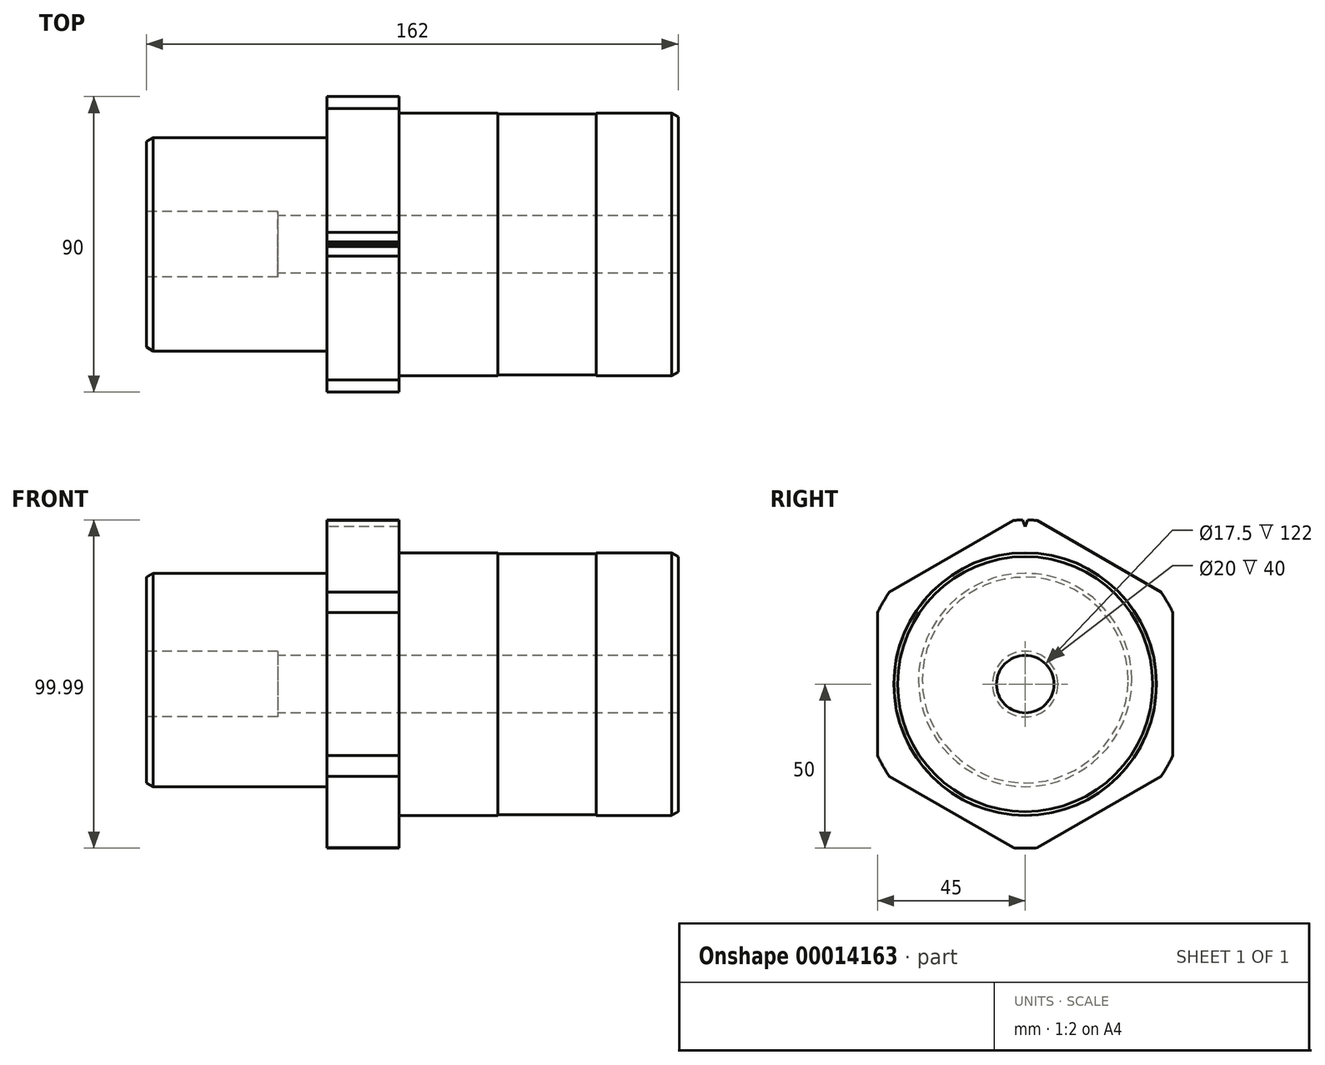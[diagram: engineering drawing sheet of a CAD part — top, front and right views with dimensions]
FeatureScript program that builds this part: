
annotation { "Feature Type Name" : "Feature", "Feature Type Description" : "" }
export const myFeature = defineFeature(function(context is Context, id is Id, definition is map)
    precondition{}
    {
        {
            var Q0;
            Q0=qCreatedBy(makeId("Right.planeOp"),FACE);
            var sketch = newSketch(context, id + "F0", { "sketchPlane" : qUnion([Q0])});
            skCircle(sketch, "E0", {"center": v(0, 0) * mm, "radius": 40 * mm});
            skCircle(sketch, "E1", {"center": v(0, 0) * mm, "radius": 8.75 * mm});
            skSolve(sketch);
        }
        {
            var Q0;
            Q0 = qSketchRegion(id + "F0", true);
            extrude(context, id + "F1", {"entities" : qUnion([Q0]), "depth" : (85 - 60) * mm});
        }
        {
            var Q0;
            Q0=makeQuery(id+"F1.opExtrude","CAP_FACE",FACE,{"disambiguationData":[OSD([sQuery(id+"F0.wireOp",EDGE,"E0"),sQuery(id+"F0.wireOp",EDGE,"E1")])],"isStart":true});
            var sketch = newSketch(context, id + "F2", { "sketchPlane" : qUnion([Q0])});
            skCircle(sketch, "E2", {"center": v(0, 0) * mm, "radius": 39.75 * mm});
            skCircle(sketch, "E3.0", {"center": v(0, 0) * mm, "radius": 8.75 * mm});
            skSolve(sketch);
        }
        {
            var Q0;
            Q0 = qSketchRegion(id + "F2", true);
            extrude(context, id + "F3", {"entities" : qUnion([Q0]), "operationType" : NewBodyOperationType.ADD, "depth" : 30 * mm});
        }
        {
            var Q0;
            Q0=makeQuery(id+"F3.opExtrude","CAP_FACE",FACE,{"disambiguationData":[OSD([sQuery(id+"F2.wireOp",EDGE,"E2"),sQuery(id+"F2.wireOp",EDGE,"E3.0")])],"isStart":false});
            var sketch = newSketch(context, id + "F4", { "sketchPlane" : qUnion([Q0])});
            skCircle(sketch, "E4", {"center": v(0, 0) * mm, "radius": 40 * mm});
            skCircle(sketch, "E5.0", {"center": v(0, 0) * mm, "radius": 8.75 * mm});
            skSolve(sketch);
        }
        {
            var Q0;
            Q0 = qSketchRegion(id + "F4", true);
            extrude(context, id + "F5", {"entities" : qUnion([Q0]), "operationType" : NewBodyOperationType.ADD, "depth" : 30 * mm});
        }
        {
            var Q0;
            Q0=makeQuery(id+"F5.opExtrude","CAP_FACE",FACE,{"disambiguationData":[OSD([sQuery(id+"F4.wireOp",EDGE,"E4"),sQuery(id+"F4.wireOp",EDGE,"E5.0")])],"isStart":false});
            var sketch = newSketch(context, id + "F6", { "sketchPlane" : qUnion([Q0])});
            skCircle(sketch, "E6.cCircle", {"center": v(0, 0) * mm, "radius": 45 * mm, "construction": true});
            skLineSegment(sketch, "E6.0", {"start": v(-45, -21.8) * mm, "end": v(-45, 21.8) * mm});
            skLineSegment(sketch, "E6.1", {"start": v(-41.37, 28.07) * mm, "end": v(-3.63, 49.87) * mm});
            skLineSegment(sketch, "E6.2", {"start": v(3.63, 49.87) * mm, "end": v(41.37, 28.07) * mm});
            skLineSegment(sketch, "E6.3", {"start": v(45, 21.8) * mm, "end": v(45, -21.8) * mm});
            skLineSegment(sketch, "E6.4", {"start": v(41.37, -28.07) * mm, "end": v(3.63, -49.87) * mm});
            skLineSegment(sketch, "E6.5", {"start": v(-3.63, -49.87) * mm, "end": v(-41.37, -28.07) * mm});
            skPoint(sketch, "E6.0.midPoint", {"position": v(-45, 0) * mm});
            skCircle(sketch, "E7.0", {"center": v(0, 0) * mm, "radius": 8.75 * mm});
            skArc(sketch, "E8", {"start": v(-3.63, -49.87) * mm, "mid": v(0, -50) * mm, "end": v(3.63, -49.87) * mm});
            skPoint(sketch, "E9.orphan", {"position": v(-45, -25.98) * mm});
            skArc(sketch, "E10.trimOffspring", {"start": v(-45, -21.8) * mm, "mid": v(-43.3, -25) * mm, "end": v(-41.37, -28.07) * mm});
            skPoint(sketch, "E11.orphan", {"position": v(-45, 25.98) * mm});
            skArc(sketch, "E12.trimOffspring", {"start": v(-41.37, 28.07) * mm, "mid": v(-43.3, 25) * mm, "end": v(-45, 21.8) * mm});
            skPoint(sketch, "E13.orphan", {"position": v(0, 51.96) * mm});
            skArc(sketch, "E14.trimOffspring", {"start": v(3.63, 49.87) * mm, "mid": v(0, 50) * mm, "end": v(-3.63, 49.87) * mm});
            skPoint(sketch, "E15.orphan", {"position": v(45, 25.98) * mm});
            skArc(sketch, "E16.trimOffspring", {"start": v(45, 21.8) * mm, "mid": v(43.3, 25) * mm, "end": v(41.37, 28.07) * mm});
            skPoint(sketch, "E17.orphan", {"position": v(45, -25.98) * mm});
            skArc(sketch, "E18.trimOffspring", {"start": v(41.37, -28.07) * mm, "mid": v(43.3, -25) * mm, "end": v(45, -21.8) * mm});
            skPoint(sketch, "E19.orphan", {"position": v(0, -51.96) * mm});
            skSolve(sketch);
        }
        {
            var Q0;
            Q0 = qSketchRegion(id + "F6", true);
            extrude(context, id + "F7", {"entities" : qUnion([Q0]), "operationType" : NewBodyOperationType.ADD, "depth" : 22 * mm});
        }
        {
            var Q0;
            Q0=makeQuery(id+"F7.opExtrude","CAP_FACE",FACE,{"disambiguationData":[OSD([sQuery(id+"F6.wireOp",EDGE,"E6.0"),sQuery(id+"F6.wireOp",EDGE,"E6.1"),sQuery(id+"F6.wireOp",EDGE,"E6.2"),sQuery(id+"F6.wireOp",EDGE,"E6.3"),sQuery(id+"F6.wireOp",EDGE,"E6.4"),sQuery(id+"F6.wireOp",EDGE,"E6.5"),sQuery(id+"F6.wireOp",EDGE,"E7.0"),sQuery(id+"F6.wireOp",EDGE,"E8"),sQuery(id+"F6.wireOp",EDGE,"E10.trimOffspring"),sQuery(id+"F6.wireOp",EDGE,"E12.trimOffspring"),sQuery(id+"F6.wireOp",EDGE,"E14.trimOffspring"),sQuery(id+"F6.wireOp",EDGE,"E16.trimOffspring"),sQuery(id+"F6.wireOp",EDGE,"E18.trimOffspring")])],"isStart":false});
            var sketch = newSketch(context, id + "F8", { "sketchPlane" : qUnion([Q0])});
            skLineSegment(sketch, "E20", {"start": v(0, 50) * mm, "end": v(0, 48) * mm, "construction": true});
            skLineSegment(sketch, "E21", {"start": v(0, 48) * mm, "end": v(-1.95, 53.35) * mm});
            skLineSegment(sketch, "E22.0.MirrorCS", {"start": v(0, 48) * mm, "end": v(1.95, 53.35) * mm});
            skLineSegment(sketch, "E23", {"start": v(-1.95, 53.35) * mm, "end": v(1.95, 53.35) * mm});
            skSolve(sketch);
        }
        {
            var Q0;
            Q0 = qSketchRegion(id + "F8", true);
            extrude(context, id + "F9", {"entities" : qUnion([Q0]), "operationType" : NewBodyOperationType.REMOVE, "oppositeDirection" : true, "depth" : 25 * mm});
        }
        {
            var Q0;
            Q0=makeQuery(id+"F7.opExtrude","CAP_FACE",FACE,{"disambiguationData":[OSD([sQuery(id+"F6.wireOp",EDGE,"E6.0"),sQuery(id+"F6.wireOp",EDGE,"E6.1"),sQuery(id+"F6.wireOp",EDGE,"E6.2"),sQuery(id+"F6.wireOp",EDGE,"E6.3"),sQuery(id+"F6.wireOp",EDGE,"E6.4"),sQuery(id+"F6.wireOp",EDGE,"E6.5"),sQuery(id+"F6.wireOp",EDGE,"E7.0"),sQuery(id+"F6.wireOp",EDGE,"E8"),sQuery(id+"F6.wireOp",EDGE,"E10.trimOffspring"),sQuery(id+"F6.wireOp",EDGE,"E12.trimOffspring"),sQuery(id+"F6.wireOp",EDGE,"E14.trimOffspring"),sQuery(id+"F6.wireOp",EDGE,"E16.trimOffspring"),sQuery(id+"F6.wireOp",EDGE,"E18.trimOffspring")])],"isStart":false});
            var sketch = newSketch(context, id + "F10", { "sketchPlane" : qUnion([Q0])});
            skLineSegment(sketch, "E24", {"start": v(0, 0) * mm, "end": v(0, 1.25) * mm, "construction": true});
            skCircle(sketch, "E25", {"center": v(0, 1.25) * mm, "radius": 32.5 * mm});
            skSolve(sketch);
        }
        {
            var Q0;
            Q0 = qSketchRegion(id + "F10", true);
            extrude(context, id + "F11", {"entities" : qUnion([Q0]), "operationType" : NewBodyOperationType.ADD, "depth" : 55 * mm});
        }
        {
            var Q0;
            Q0=makeQuery(id+"F11.opExtrude","CAP_FACE",FACE,{"disambiguationData":[OSD([sQuery(id+"F10.wireOp",EDGE,"E25")])],"isStart":false});
            var sketch = newSketch(context, id + "F12", { "sketchPlane" : qUnion([Q0])});
            skLineSegment(sketch, "E26", {"start": v(0, 0) * mm, "end": v(-58.41, 0) * mm, "construction": true});
            skSolve(sketch);
        }
        {
            var Q0;
            Q0=sQuery(id+"F12.wireOp",VERTEX,"E26.start");
            var Q1;
            Q1=makeQuery(id+"F1.opExtrude","SWEPT_BODY",BODY,{"disambiguationData":[OSD([sQuery(id+"F0.wireOp",EDGE,"E0"),sQuery(id+"F0.wireOp",EDGE,"E1")])]});
            hole(context, id + "F13", {"style" : HoleStyle.C_BORE, "holeDiameter" : 17.5 * mm, "cBoreDiameter" : 20 * mm, "cBoreDepth" : 40 * mm, "endStyle" : HoleEndStyle.THROUGH, "locations" : qUnion([Q0]), "scope" : qUnion([Q1])});
        }
        {
            var Q0;
            Q0=makeQuery(id+"F11.opExtrude","CAP_EDGE",EDGE,{"disambiguationData":[OSD([sQuery(id+"F10.wireOp",EDGE,"E25")])],"isStart":false});
            var Q1;
            Q1=makeQuery(id+"F1.opExtrude","CAP_EDGE",EDGE,{"disambiguationData":[OSD([sQuery(id+"F0.wireOp",EDGE,"E0")])],"isStart":false});
            chamfer(context, id + "F14", {"entities" : qUnion([Q0, Q1]), "chamferType" : ChamferType.OFFSET_ANGLE, "width" : 2 * mm, "oppositeDirection" : true, "angle" : 30 * degree, "tangentPropagation" : true});
        }
    });
